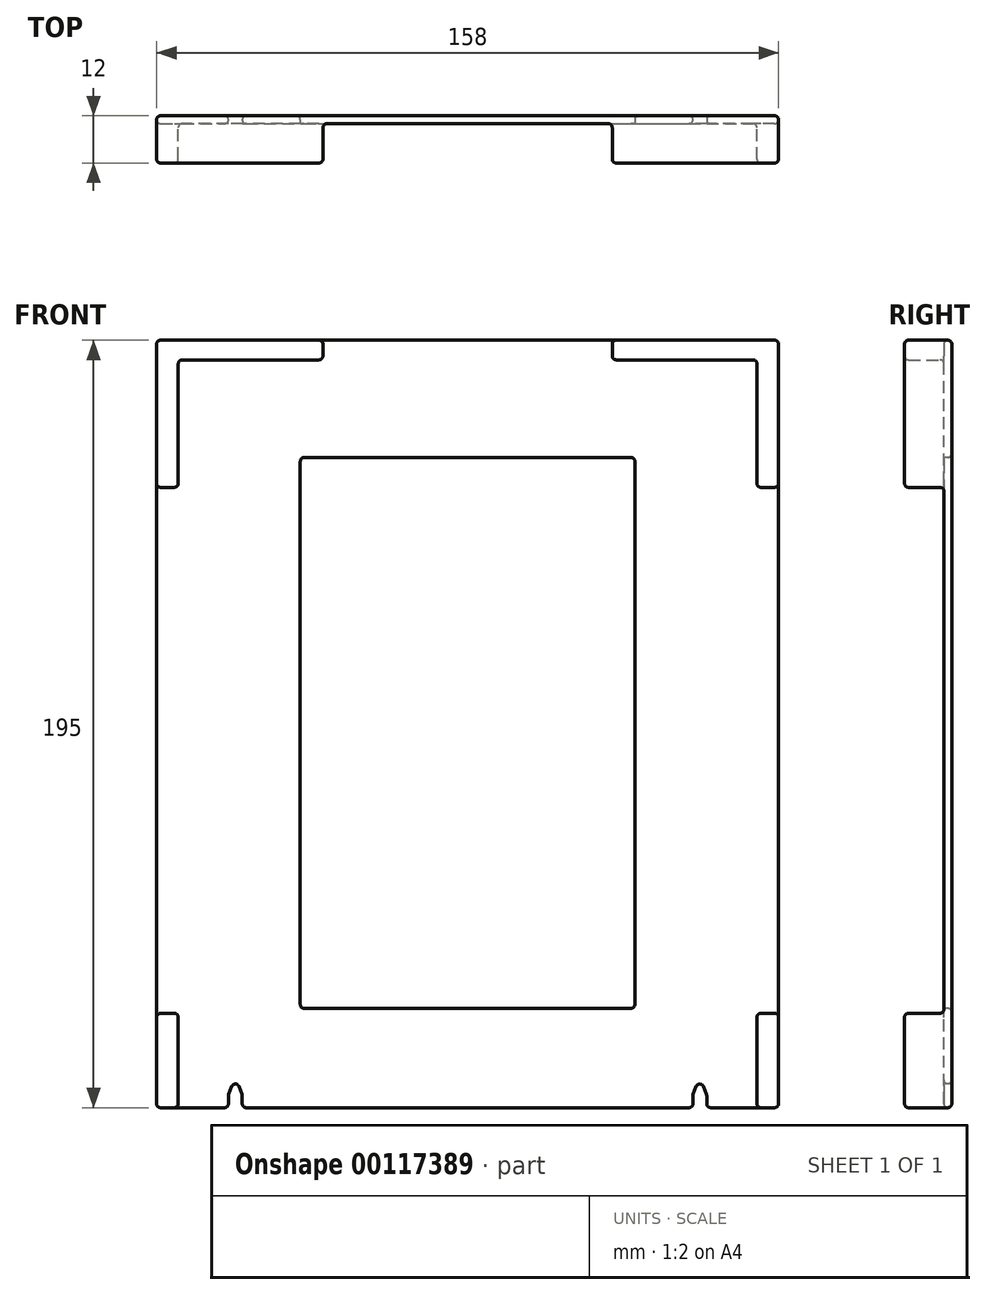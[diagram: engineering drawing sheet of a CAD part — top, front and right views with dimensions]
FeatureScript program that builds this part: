
annotation { "Feature Type Name" : "Feature", "Feature Type Description" : "" }
export const myFeature = defineFeature(function(context is Context, id is Id, definition is map)
    precondition{}
    {
        {
            var Q0;
            Q0=qCreatedBy(makeId("Front.planeOp"),FACE);
            var sketch = newSketch(context, id + "F0", { "sketchPlane" : qUnion([Q0])});
            skLineSegment(sketch, "E0.top", {"start": v(-73.5, 185) * mm, "end": v(-36.75, 185) * mm});
            skLineSegment(sketch, "E1.0", {"start": v(-79, 190) * mm, "end": v(0, 190) * mm});
            skLineSegment(sketch, "E1.1", {"start": v(-79, -5) * mm, "end": v(-79, 190) * mm});
            skLineSegment(sketch, "E1.2", {"start": v(-79, -5) * mm, "end": v(-60.75, -5) * mm});
            skLineSegment(sketch, "E2", {"start": v(-57.25, -1.81) * mm, "end": v(-57.25, -5) * mm});
            skLineSegment(sketch, "E3", {"start": v(-60.75, -1.81) * mm, "end": v(-60.75, -5) * mm});
            skLineSegment(sketch, "E4.trimOffspring", {"start": v(-57.25, -5) * mm, "end": v(0, -5) * mm});
            skArc(sketch, "E5", {"start": v(-58.06, 0.35) * mm, "mid": v(-59, 1) * mm, "end": v(-59.94, 0.35) * mm});
            skLineSegment(sketch, "E6", {"start": v(-58.06, 0.35) * mm, "end": v(-57.25, -1.81) * mm});
            skLineSegment(sketch, "E7", {"start": v(-59, 0) * mm, "end": v(-59, -2.66) * mm, "construction": true});
            skLineSegment(sketch, "E8.MirrorCS", {"start": v(-59.94, 0.35) * mm, "end": v(-60.75, -1.81) * mm});
            skLineSegment(sketch, "E9", {"start": v(0, -9.83) * mm, "end": v(0, 204.68) * mm, "construction": true});
            skPoint(sketch, "E9.startSnap0", {"position": v(0, -5) * mm});
            skLineSegment(sketch, "E10", {"start": v(-73.5, 185) * mm, "end": v(-73.5, 152.6) * mm});
            skLineSegment(sketch, "E11", {"start": v(-36.75, 185) * mm, "end": v(-36.75, 190) * mm});
            skLineSegment(sketch, "E12", {"start": v(-73.5, 152.6) * mm, "end": v(-79, 152.6) * mm});
            skLineSegment(sketch, "E13", {"start": v(-73.5, 18.97) * mm, "end": v(-79, 18.97) * mm});
            skPoint(sketch, "E14.orphan", {"position": v(0, 185) * mm});
            skLineSegment(sketch, "E15.trimOffspring", {"start": v(-73.5, 18.97) * mm, "end": v(-73.5, -5) * mm});
            skArc(sketch, "E16.MirrorCS", {"start": v(58.06, 0.35) * mm, "mid": v(59, 1) * mm, "end": v(59.94, 0.35) * mm});
            skLineSegment(sketch, "E17.MirrorCS", {"start": v(60.75, -1.81) * mm, "end": v(60.75, -5) * mm});
            skLineSegment(sketch, "E18.MirrorCS", {"start": v(57.25, -1.81) * mm, "end": v(57.25, -5) * mm});
            skLineSegment(sketch, "E19.MirrorCS", {"start": v(59.94, 0.35) * mm, "end": v(60.75, -1.81) * mm});
            skLineSegment(sketch, "E20.MirrorCS", {"start": v(59, 0) * mm, "end": v(59, -2.66) * mm, "construction": true});
            skLineSegment(sketch, "E21.MirrorCS", {"start": v(58.06, 0.35) * mm, "end": v(57.25, -1.81) * mm});
            skLineSegment(sketch, "E22.MirrorCS", {"start": v(73.5, 152.6) * mm, "end": v(79, 152.6) * mm});
            skLineSegment(sketch, "E23.MirrorCS", {"start": v(36.75, 185) * mm, "end": v(36.75, 190) * mm});
            skLineSegment(sketch, "E24.MirrorCS", {"start": v(73.5, 18.97) * mm, "end": v(79, 18.97) * mm});
            skLineSegment(sketch, "E25.MirrorCS", {"start": v(79, -5) * mm, "end": v(60.75, -5) * mm});
            skLineSegment(sketch, "E26.MirrorCS", {"start": v(73.5, 185) * mm, "end": v(73.5, 152.6) * mm});
            skLineSegment(sketch, "E27.MirrorCS", {"start": v(79, -5) * mm, "end": v(79, 190) * mm});
            skLineSegment(sketch, "E28.MirrorCS", {"start": v(79, 190) * mm, "end": v(0, 190) * mm});
            skLineSegment(sketch, "E29.MirrorCS", {"start": v(73.5, 185) * mm, "end": v(36.75, 185) * mm});
            skLineSegment(sketch, "E30.MirrorCS", {"start": v(57.25, -5) * mm, "end": v(0, -5) * mm});
            skLineSegment(sketch, "E31.MirrorCS", {"start": v(73.5, 18.97) * mm, "end": v(73.5, -5) * mm});
            skSolve(sketch);
        }
        {
            var Q0;
            Q0=makeQuery(id+"F0.imprint","IMPRINT",FACE,{"disambiguationData":[TD([[makeQuery(id+"F0.imprint","IMPRINT",EDGE,{"derivedFrom":sQuery(id+"F0.wireOp",EDGE,"E0.top")}),-1.0]])]});
            var Q1;
            Q1=makeQuery(id+"F0.imprint","IMPRINT",FACE,{"disambiguationData":[TD([[makeQuery(id+"F0.imprint","IMPRINT",EDGE,{"derivedFrom":sQuery(id+"F0.wireOp",EDGE,"E0.top")}),1.0]])]});
            var Q2;
            {var subQ1=sQuery(id+"F0.wireOp",EDGE,"E22.MirrorCS");Q2=makeQuery(id+"F0.imprint","IMPRINT",FACE,{"disambiguationData":[TD([[makeQuery(id+"F0.imprint","IMPRINT",EDGE,{"derivedFrom":subQ1}),1.0]])]});}
            var Q3;
            {var subQ0=sQuery(id+"F0.wireOp",EDGE,"E24.MirrorCS");Q3=makeQuery(id+"F0.imprint","IMPRINT",FACE,{"disambiguationData":[TD([[makeQuery(id+"F0.imprint","IMPRINT",EDGE,{"derivedFrom":subQ0}),-1.0]])]});}
            var Q4;
            {var subQ3=sQuery(id+"F0.wireOp",EDGE,"E13");Q4=makeQuery(id+"F0.imprint","IMPRINT",FACE,{"disambiguationData":[TD([[makeQuery(id+"F0.imprint","IMPRINT",EDGE,{"derivedFrom":subQ3}),1.0]])]});}
            extrude(context, id + "F1", {"entities" : qUnion([Q0, Q1, Q2, Q3, Q4]), "depth" : 2 * mm});
        }
        {
            var Q0;
            {var subQ1=sQuery(id+"F0.wireOp",EDGE,"E22.MirrorCS");Q0=makeQuery(id+"F0.imprint","IMPRINT",FACE,{"disambiguationData":[TD([[makeQuery(id+"F0.imprint","IMPRINT",EDGE,{"derivedFrom":subQ1}),1.0]])]});}
            var Q1;
            Q1=makeQuery(id+"F0.imprint","IMPRINT",FACE,{"disambiguationData":[TD([[makeQuery(id+"F0.imprint","IMPRINT",EDGE,{"derivedFrom":sQuery(id+"F0.wireOp",EDGE,"E0.top")}),1.0]])]});
            var Q2;
            {var subQ3=sQuery(id+"F0.wireOp",EDGE,"E13");Q2=makeQuery(id+"F0.imprint","IMPRINT",FACE,{"disambiguationData":[TD([[makeQuery(id+"F0.imprint","IMPRINT",EDGE,{"derivedFrom":subQ3}),1.0]])]});}
            var Q3;
            {var subQ0=sQuery(id+"F0.wireOp",EDGE,"E24.MirrorCS");Q3=makeQuery(id+"F0.imprint","IMPRINT",FACE,{"disambiguationData":[TD([[makeQuery(id+"F0.imprint","IMPRINT",EDGE,{"derivedFrom":subQ0}),-1.0]])]});}
            extrude(context, id + "F2", {"entities" : qUnion([Q0, Q1, Q2, Q3]), "operationType" : NewBodyOperationType.ADD, "depth" : 12 * mm});
        }
        {
            var Q0;
            Q0=makeQuery(id+"F1.opExtrude","CAP_FACE",FACE,{"disambiguationData":[OSD([sQuery(id+"F0.wireOp",EDGE,"E1.0"),sQuery(id+"F0.wireOp",EDGE,"E1.1"),sQuery(id+"F0.wireOp",EDGE,"E1.2"),sQuery(id+"F0.wireOp",EDGE,"E2"),sQuery(id+"F0.wireOp",EDGE,"E3"),sQuery(id+"F0.wireOp",EDGE,"E4.trimOffspring"),sQuery(id+"F0.wireOp",EDGE,"E5"),sQuery(id+"F0.wireOp",EDGE,"E6"),sQuery(id+"F0.wireOp",EDGE,"E8.MirrorCS"),sQuery(id+"F0.wireOp",EDGE,"E16.MirrorCS"),sQuery(id+"F0.wireOp",EDGE,"E17.MirrorCS"),sQuery(id+"F0.wireOp",EDGE,"E18.MirrorCS"),sQuery(id+"F0.wireOp",EDGE,"E19.MirrorCS"),sQuery(id+"F0.wireOp",EDGE,"E21.MirrorCS"),sQuery(id+"F0.wireOp",EDGE,"E25.MirrorCS"),sQuery(id+"F0.wireOp",EDGE,"E27.MirrorCS"),sQuery(id+"F0.wireOp",EDGE,"E28.MirrorCS"),sQuery(id+"F0.wireOp",EDGE,"E30.MirrorCS")])],"isStart":false});
            var sketch = newSketch(context, id + "F3", { "sketchPlane" : qUnion([Q0])});
            skLineSegment(sketch, "E32.bottom", {"start": v(-42.5, 160.22) * mm, "end": v(42.5, 160.22) * mm});
            skLineSegment(sketch, "E32.top", {"start": v(-42.5, 20.22) * mm, "end": v(42.5, 20.22) * mm});
            skLineSegment(sketch, "E32.left", {"start": v(-42.5, 160.22) * mm, "end": v(-42.5, 20.22) * mm});
            skLineSegment(sketch, "E32.right", {"start": v(42.5, 160.22) * mm, "end": v(42.5, 20.22) * mm});
            skSolve(sketch);
        }
        {
            var Q0;
            Q0 = qSketchRegion(id + "F3", true);
            extrude(context, id + "F4", {"entities" : qUnion([Q0]), "operationType" : NewBodyOperationType.REMOVE, "oppositeDirection" : true, "depth" : 25 * mm});
        }
        {
            var Q0;
            Q0=makeQuery(id+"F2.opExtrude","CAP_EDGE",EDGE,{"disambiguationData":[OSD([sQuery(id+"F0.wireOp",EDGE,"E29.MirrorCS")])],"isStart":false});
            var Q1;
            Q1=makeQuery(id+"F2.opExtrude","CAP_EDGE",EDGE,{"disambiguationData":[OSD([sQuery(id+"F0.wireOp",EDGE,"E10")])],"isStart":false});
            var Q2;
            Q2=makeQuery(id+"F4.boolean.opBoolean","COPY",EDGE,{"derivedFrom":makeQuery(id+"F4.opExtrude","CAP_EDGE",EDGE,{"disambiguationData":[OSD([sQuery(id+"F3.wireOp",EDGE,"E32.top")])],"isStart":true})});
            var Q3;
            Q3=makeQuery(id+"F2.opExtrude","CAP_EDGE",EDGE,{"disambiguationData":[OSD([sQuery(id+"F0.wireOp",EDGE,"E1.0")])],"isStart":false});
            var Q4;
            Q4=makeQuery(id+"F2.opExtrude","CAP_EDGE",EDGE,{"disambiguationData":[OSD([sQuery(id+"F0.wireOp",EDGE,"E28.MirrorCS")])],"isStart":false});
            var Q5;
            Q5=makeQuery(id+"F2.opExtrude","CAP_EDGE",EDGE,{"disambiguationData":[OSD([sQuery(id+"F0.wireOp",EDGE,"E31.MirrorCS")])],"isStart":false});
            var Q6;
            {var subQ0=sQuery(id+"F0.wireOp",EDGE,"E1.1");Q6=makeQuery(id+"F2.opExtrude","CAP_EDGE",EDGE,{"disambiguationData":[OSD([subQ0]),TDD([makeQuery(id+"F0.imprint","IMPRINT",EDGE,{"disambiguationData":[TD([[makeQuery(id+"F0.imprint","INTERSECT",VERTEX,{"derivedFrom":[sQuery(id+"F0.wireOp",EDGE,"E1.0"),subQ0]}),1.0]])],"derivedFrom":subQ0})])],"isStart":false});}
            var Q7;
            Q7=makeQuery(id+"F2.opExtrude","CAP_EDGE",EDGE,{"disambiguationData":[OSD([sQuery(id+"F0.wireOp",EDGE,"E23.MirrorCS")])],"isStart":false});
            var Q8;
            Q8=makeQuery(id+"F2.opExtrude","CAP_EDGE",EDGE,{"disambiguationData":[OSD([sQuery(id+"F0.wireOp",EDGE,"E15.trimOffspring")])],"isStart":false});
            var Q9;
            Q9=makeQuery(id+"F2.opExtrude","CAP_EDGE",EDGE,{"disambiguationData":[OSD([sQuery(id+"F0.wireOp",EDGE,"E24.MirrorCS")])],"isStart":false});
            var Q10;
            Q10=makeQuery(id+"F1.opExtrude","CAP_EDGE",EDGE,{"disambiguationData":[OSD([sQuery(id+"F0.wireOp",EDGE,"E17.MirrorCS")])],"isStart":false});
            var Q11;
            Q11=makeQuery(id+"F2.opExtrude","CAP_EDGE",EDGE,{"disambiguationData":[OSD([sQuery(id+"F0.wireOp",EDGE,"E1.2")])],"isStart":false});
            var Q12;
            Q12=makeQuery(id+"F1.opExtrude","SWEPT_EDGE",EDGE,{"disambiguationData":[OSD([sQuery(id+"F0.wireOp",EDGE,"E1.2"),sQuery(id+"F0.wireOp",EDGE,"E3")])]});
            var Q13;
            Q13=makeQuery(id+"F2.opExtrude","SWEPT_EDGE",EDGE,{"disambiguationData":[OSD([sQuery(id+"F0.wireOp",EDGE,"E26.MirrorCS"),sQuery(id+"F0.wireOp",EDGE,"E29.MirrorCS")])]});
            var Q14;
            Q14=makeQuery(id+"F1.opExtrude","CAP_EDGE",EDGE,{"disambiguationData":[OSD([sQuery(id+"F0.wireOp",EDGE,"E2")])],"isStart":false});
            var Q15;
            Q15=makeQuery(id+"F1.opExtrude","CAP_EDGE",EDGE,{"disambiguationData":[OSD([sQuery(id+"F0.wireOp",EDGE,"E4.trimOffspring"),sQuery(id+"F0.wireOp",EDGE,"E30.MirrorCS")])],"isStart":false});
            var Q16;
            Q16=makeQuery(id+"F2.opExtrude","CAP_EDGE",EDGE,{"disambiguationData":[OSD([sQuery(id+"F0.wireOp",EDGE,"E13")])],"isStart":false});
            var Q17;
            Q17=makeQuery(id+"F2.opExtrude","CAP_EDGE",EDGE,{"disambiguationData":[OSD([sQuery(id+"F0.wireOp",EDGE,"E0.top")])],"isStart":false});
            var Q18;
            {var subQ0=sQuery(id+"F0.wireOp",EDGE,"E27.MirrorCS");Q18=makeQuery(id+"F2.opExtrude","CAP_EDGE",EDGE,{"disambiguationData":[OSD([subQ0]),TDD([makeQuery(id+"F0.imprint","IMPRINT",EDGE,{"disambiguationData":[TD([[makeQuery(id+"F0.imprint","INTERSECT",VERTEX,{"derivedFrom":[sQuery(id+"F0.wireOp",EDGE,"E22.MirrorCS"),subQ0]}),-1.0]])],"derivedFrom":subQ0})])],"isStart":false});}
            var Q19;
            Q19=makeQuery(id+"F2.opExtrude","CAP_EDGE",EDGE,{"disambiguationData":[OSD([sQuery(id+"F0.wireOp",EDGE,"E26.MirrorCS")])],"isStart":false});
            var Q20;
            Q20=makeQuery(id+"F1.opExtrude","CAP_EDGE",EDGE,{"disambiguationData":[OSD([sQuery(id+"F0.wireOp",EDGE,"E27.MirrorCS")])],"isStart":false});
            var Q21;
            {var subQ0=sQuery(id+"F0.wireOp",EDGE,"E1.1");Q21=makeQuery(id+"F2.opExtrude","CAP_EDGE",EDGE,{"disambiguationData":[OSD([subQ0]),TDD([makeQuery(id+"F0.imprint","IMPRINT",EDGE,{"disambiguationData":[TD([[makeQuery(id+"F0.imprint","INTERSECT",VERTEX,{"derivedFrom":[subQ0,sQuery(id+"F0.wireOp",EDGE,"E1.2")]}),-1.0]])],"derivedFrom":subQ0})])],"isStart":false});}
            var Q22;
            Q22=makeQuery(id+"F1.opExtrude","CAP_EDGE",EDGE,{"disambiguationData":[OSD([sQuery(id+"F0.wireOp",EDGE,"E1.0"),sQuery(id+"F0.wireOp",EDGE,"E28.MirrorCS")])],"isStart":false});
            var Q23;
            Q23=makeQuery(id+"F1.opExtrude","CAP_EDGE",EDGE,{"disambiguationData":[OSD([sQuery(id+"F0.wireOp",EDGE,"E1.1")])],"isStart":false});
            var Q24;
            Q24=makeQuery(id+"F2.opExtrude","CAP_EDGE",EDGE,{"disambiguationData":[OSD([sQuery(id+"F0.wireOp",EDGE,"E25.MirrorCS")])],"isStart":false});
            var Q25;
            Q25=makeQuery(id+"F1.opExtrude","CAP_EDGE",EDGE,{"disambiguationData":[OSD([sQuery(id+"F0.wireOp",EDGE,"E1.2")])],"isStart":false});
            var Q26;
            Q26=makeQuery(id+"F1.opExtrude","CAP_EDGE",EDGE,{"disambiguationData":[OSD([sQuery(id+"F0.wireOp",EDGE,"E25.MirrorCS")])],"isStart":false});
            var Q27;
            Q27=makeQuery(id+"F2.opExtrude","CAP_EDGE",EDGE,{"disambiguationData":[OSD([sQuery(id+"F0.wireOp",EDGE,"E12")])],"isStart":false});
            var Q28;
            {var subQ0=sQuery(id+"F0.wireOp",EDGE,"E27.MirrorCS");Q28=makeQuery(id+"F2.opExtrude","CAP_EDGE",EDGE,{"disambiguationData":[OSD([subQ0]),TDD([makeQuery(id+"F0.imprint","IMPRINT",EDGE,{"disambiguationData":[TD([[makeQuery(id+"F0.imprint","INTERSECT",VERTEX,{"derivedFrom":[sQuery(id+"F0.wireOp",EDGE,"E24.MirrorCS"),subQ0]}),1.0]])],"derivedFrom":subQ0})])],"isStart":false});}
            var Q29;
            Q29=makeQuery(id+"F4.boolean.opBoolean","COPY",EDGE,{"derivedFrom":makeQuery(id+"F4.opExtrude","SWEPT_EDGE",EDGE,{"disambiguationData":[OSD([sQuery(id+"F3.wireOp",EDGE,"E32.top"),sQuery(id+"F3.wireOp",EDGE,"E32.left")])]})});
            var Q30;
            Q30=makeQuery(id+"F4.boolean.opBoolean","COPY",EDGE,{"derivedFrom":makeQuery(id+"F4.opExtrude","SWEPT_EDGE",EDGE,{"disambiguationData":[OSD([sQuery(id+"F3.wireOp",EDGE,"E32.top"),sQuery(id+"F3.wireOp",EDGE,"E32.right")])]})});
            var Q31;
            Q31=makeQuery(id+"F4.boolean.opBoolean","COPY",EDGE,{"derivedFrom":makeQuery(id+"F4.opExtrude","CAP_EDGE",EDGE,{"disambiguationData":[OSD([sQuery(id+"F3.wireOp",EDGE,"E32.bottom")])],"isStart":true})});
            var Q32;
            Q32=makeQuery(id+"F4.boolean.opBoolean","COPY",EDGE,{"derivedFrom":makeQuery(id+"F4.opExtrude","CAP_EDGE",EDGE,{"disambiguationData":[OSD([sQuery(id+"F3.wireOp",EDGE,"E32.left")])],"isStart":true})});
            var Q33;
            Q33=makeQuery(id+"F4.boolean.opBoolean","COPY",EDGE,{"derivedFrom":makeQuery(id+"F4.opExtrude","CAP_EDGE",EDGE,{"disambiguationData":[OSD([sQuery(id+"F3.wireOp",EDGE,"E32.right")])],"isStart":true})});
            var Q34;
            Q34=makeQuery(id+"F1.opExtrude","CAP_EDGE",EDGE,{"disambiguationData":[OSD([sQuery(id+"F0.wireOp",EDGE,"E6")])],"isStart":false});
            var Q35;
            Q35=makeQuery(id+"F1.opExtrude","SWEPT_EDGE",EDGE,{"disambiguationData":[OSD([sQuery(id+"F0.wireOp",EDGE,"E2"),sQuery(id+"F0.wireOp",EDGE,"E4.trimOffspring")])]});
            var Q36;
            Q36=makeQuery(id+"F1.opExtrude","CAP_EDGE",EDGE,{"disambiguationData":[OSD([sQuery(id+"F0.wireOp",EDGE,"E2")])],"isStart":true});
            var Q37;
            Q37=makeQuery(id+"F1.opExtrude","CAP_EDGE",EDGE,{"disambiguationData":[OSD([sQuery(id+"F0.wireOp",EDGE,"E4.trimOffspring"),sQuery(id+"F0.wireOp",EDGE,"E30.MirrorCS")])],"isStart":true});
            var Q38;
            Q38=makeQuery(id+"F1.opExtrude","CAP_EDGE",EDGE,{"disambiguationData":[OSD([sQuery(id+"F0.wireOp",EDGE,"E3")])],"isStart":false});
            var Q39;
            Q39=makeQuery(id+"F1.opExtrude","CAP_EDGE",EDGE,{"disambiguationData":[OSD([sQuery(id+"F0.wireOp",EDGE,"E16.MirrorCS")])],"isStart":false});
            var Q40;
            Q40=makeQuery(id+"F1.opExtrude","CAP_EDGE",EDGE,{"disambiguationData":[OSD([sQuery(id+"F0.wireOp",EDGE,"E8.MirrorCS")])],"isStart":false});
            var Q41;
            Q41=makeQuery(id+"F1.opExtrude","SWEPT_EDGE",EDGE,{"disambiguationData":[OSD([sQuery(id+"F0.wireOp",EDGE,"E17.MirrorCS"),sQuery(id+"F0.wireOp",EDGE,"E25.MirrorCS")])]});
            var Q42;
            Q42=makeQuery(id+"F1.opExtrude","SWEPT_EDGE",EDGE,{"disambiguationData":[OSD([sQuery(id+"F0.wireOp",EDGE,"E17.MirrorCS"),sQuery(id+"F0.wireOp",EDGE,"E19.MirrorCS")])]});
            var Q43;
            Q43=makeQuery(id+"F1.opExtrude","CAP_EDGE",EDGE,{"disambiguationData":[OSD([sQuery(id+"F0.wireOp",EDGE,"E19.MirrorCS")])],"isStart":false});
            var Q44;
            Q44=makeQuery(id+"F1.opExtrude","SWEPT_EDGE",EDGE,{"disambiguationData":[OSD([sQuery(id+"F0.wireOp",EDGE,"E2"),sQuery(id+"F0.wireOp",EDGE,"E6")])]});
            var Q45;
            Q45=makeQuery(id+"F2.boolean.opBoolean","INTERSECT",EDGE,{"derivedFrom":[makeQuery(id+"F1.opExtrude","CAP_FACE",FACE,{"disambiguationData":[OSD([sQuery(id+"F0.wireOp",EDGE,"E1.0"),sQuery(id+"F0.wireOp",EDGE,"E1.1"),sQuery(id+"F0.wireOp",EDGE,"E1.2"),sQuery(id+"F0.wireOp",EDGE,"E2"),sQuery(id+"F0.wireOp",EDGE,"E3"),sQuery(id+"F0.wireOp",EDGE,"E4.trimOffspring"),sQuery(id+"F0.wireOp",EDGE,"E5"),sQuery(id+"F0.wireOp",EDGE,"E6"),sQuery(id+"F0.wireOp",EDGE,"E8.MirrorCS"),sQuery(id+"F0.wireOp",EDGE,"E16.MirrorCS"),sQuery(id+"F0.wireOp",EDGE,"E17.MirrorCS"),sQuery(id+"F0.wireOp",EDGE,"E18.MirrorCS"),sQuery(id+"F0.wireOp",EDGE,"E19.MirrorCS"),sQuery(id+"F0.wireOp",EDGE,"E21.MirrorCS"),sQuery(id+"F0.wireOp",EDGE,"E25.MirrorCS"),sQuery(id+"F0.wireOp",EDGE,"E27.MirrorCS"),sQuery(id+"F0.wireOp",EDGE,"E28.MirrorCS"),sQuery(id+"F0.wireOp",EDGE,"E30.MirrorCS")])],"isStart":false}),makeQuery(id+"F2.opExtrude","SWEPT_FACE",FACE,{"disambiguationData":[OSD([sQuery(id+"F0.wireOp",EDGE,"E29.MirrorCS")])]})]});
            var Q46;
            Q46=makeQuery(id+"F2.opExtrude","SWEPT_EDGE",EDGE,{"disambiguationData":[OSD([sQuery(id+"F0.wireOp",EDGE,"E23.MirrorCS"),sQuery(id+"F0.wireOp",EDGE,"E29.MirrorCS")])]});
            var Q47;
            Q47=makeQuery(id+"F2.opExtrude","SWEPT_EDGE",EDGE,{"disambiguationData":[OSD([sQuery(id+"F0.wireOp",EDGE,"E1.2"),sQuery(id+"F0.wireOp",EDGE,"E15.trimOffspring")])]});
            var Q48;
            Q48=makeQuery(id+"F1.opExtrude","CAP_EDGE",EDGE,{"disambiguationData":[OSD([sQuery(id+"F0.wireOp",EDGE,"E5")])],"isStart":false});
            var Q49;
            Q49=makeQuery(id+"F2.boolean.opBoolean","INTERSECT",EDGE,{"derivedFrom":[makeQuery(id+"F1.opExtrude","CAP_FACE",FACE,{"disambiguationData":[OSD([sQuery(id+"F0.wireOp",EDGE,"E1.0"),sQuery(id+"F0.wireOp",EDGE,"E1.1"),sQuery(id+"F0.wireOp",EDGE,"E1.2"),sQuery(id+"F0.wireOp",EDGE,"E2"),sQuery(id+"F0.wireOp",EDGE,"E3"),sQuery(id+"F0.wireOp",EDGE,"E4.trimOffspring"),sQuery(id+"F0.wireOp",EDGE,"E5"),sQuery(id+"F0.wireOp",EDGE,"E6"),sQuery(id+"F0.wireOp",EDGE,"E8.MirrorCS"),sQuery(id+"F0.wireOp",EDGE,"E16.MirrorCS"),sQuery(id+"F0.wireOp",EDGE,"E17.MirrorCS"),sQuery(id+"F0.wireOp",EDGE,"E18.MirrorCS"),sQuery(id+"F0.wireOp",EDGE,"E19.MirrorCS"),sQuery(id+"F0.wireOp",EDGE,"E21.MirrorCS"),sQuery(id+"F0.wireOp",EDGE,"E25.MirrorCS"),sQuery(id+"F0.wireOp",EDGE,"E27.MirrorCS"),sQuery(id+"F0.wireOp",EDGE,"E28.MirrorCS"),sQuery(id+"F0.wireOp",EDGE,"E30.MirrorCS")])],"isStart":false}),makeQuery(id+"F2.opExtrude","SWEPT_FACE",FACE,{"disambiguationData":[OSD([sQuery(id+"F0.wireOp",EDGE,"E0.top")])]})]});
            var Q50;
            Q50=makeQuery(id+"F1.opExtrude","CAP_EDGE",EDGE,{"disambiguationData":[OSD([sQuery(id+"F0.wireOp",EDGE,"E18.MirrorCS")])],"isStart":false});
            var Q51;
            Q51=makeQuery(id+"F1.opExtrude","CAP_EDGE",EDGE,{"disambiguationData":[OSD([sQuery(id+"F0.wireOp",EDGE,"E21.MirrorCS")])],"isStart":false});
            var Q52;
            Q52=makeQuery(id+"F2.opExtrude","CAP_EDGE",EDGE,{"disambiguationData":[OSD([sQuery(id+"F0.wireOp",EDGE,"E11")])],"isStart":false});
            var Q53;
            Q53=makeQuery(id+"F2.boolean.opBoolean","INTERSECT",EDGE,{"derivedFrom":[makeQuery(id+"F1.opExtrude","CAP_FACE",FACE,{"disambiguationData":[OSD([sQuery(id+"F0.wireOp",EDGE,"E1.0"),sQuery(id+"F0.wireOp",EDGE,"E1.1"),sQuery(id+"F0.wireOp",EDGE,"E1.2"),sQuery(id+"F0.wireOp",EDGE,"E2"),sQuery(id+"F0.wireOp",EDGE,"E3"),sQuery(id+"F0.wireOp",EDGE,"E4.trimOffspring"),sQuery(id+"F0.wireOp",EDGE,"E5"),sQuery(id+"F0.wireOp",EDGE,"E6"),sQuery(id+"F0.wireOp",EDGE,"E8.MirrorCS"),sQuery(id+"F0.wireOp",EDGE,"E16.MirrorCS"),sQuery(id+"F0.wireOp",EDGE,"E17.MirrorCS"),sQuery(id+"F0.wireOp",EDGE,"E18.MirrorCS"),sQuery(id+"F0.wireOp",EDGE,"E19.MirrorCS"),sQuery(id+"F0.wireOp",EDGE,"E21.MirrorCS"),sQuery(id+"F0.wireOp",EDGE,"E25.MirrorCS"),sQuery(id+"F0.wireOp",EDGE,"E27.MirrorCS"),sQuery(id+"F0.wireOp",EDGE,"E28.MirrorCS"),sQuery(id+"F0.wireOp",EDGE,"E30.MirrorCS")])],"isStart":false}),makeQuery(id+"F2.opExtrude","SWEPT_FACE",FACE,{"disambiguationData":[OSD([sQuery(id+"F0.wireOp",EDGE,"E31.MirrorCS")])]})]});
            var Q54;
            Q54=makeQuery(id+"F2.opExtrude","SWEPT_EDGE",EDGE,{"disambiguationData":[OSD([sQuery(id+"F0.wireOp",EDGE,"E23.MirrorCS"),sQuery(id+"F0.wireOp",EDGE,"E28.MirrorCS")])]});
            var Q55;
            Q55=makeQuery(id+"F2.boolean.opBoolean","INTERSECT",EDGE,{"derivedFrom":[makeQuery(id+"F1.opExtrude","CAP_FACE",FACE,{"disambiguationData":[OSD([sQuery(id+"F0.wireOp",EDGE,"E1.0"),sQuery(id+"F0.wireOp",EDGE,"E1.1"),sQuery(id+"F0.wireOp",EDGE,"E1.2"),sQuery(id+"F0.wireOp",EDGE,"E2"),sQuery(id+"F0.wireOp",EDGE,"E3"),sQuery(id+"F0.wireOp",EDGE,"E4.trimOffspring"),sQuery(id+"F0.wireOp",EDGE,"E5"),sQuery(id+"F0.wireOp",EDGE,"E6"),sQuery(id+"F0.wireOp",EDGE,"E8.MirrorCS"),sQuery(id+"F0.wireOp",EDGE,"E16.MirrorCS"),sQuery(id+"F0.wireOp",EDGE,"E17.MirrorCS"),sQuery(id+"F0.wireOp",EDGE,"E18.MirrorCS"),sQuery(id+"F0.wireOp",EDGE,"E19.MirrorCS"),sQuery(id+"F0.wireOp",EDGE,"E21.MirrorCS"),sQuery(id+"F0.wireOp",EDGE,"E25.MirrorCS"),sQuery(id+"F0.wireOp",EDGE,"E27.MirrorCS"),sQuery(id+"F0.wireOp",EDGE,"E28.MirrorCS"),sQuery(id+"F0.wireOp",EDGE,"E30.MirrorCS")])],"isStart":false}),makeQuery(id+"F2.opExtrude","SWEPT_FACE",FACE,{"disambiguationData":[OSD([sQuery(id+"F0.wireOp",EDGE,"E10")])]})]});
            var Q56;
            Q56=makeQuery(id+"F2.opExtrude","SWEPT_EDGE",EDGE,{"disambiguationData":[OSD([sQuery(id+"F0.wireOp",EDGE,"E1.1"),sQuery(id+"F0.wireOp",EDGE,"E12")])]});
            var Q57;
            Q57=makeQuery(id+"F2.opExtrude","SWEPT_EDGE",EDGE,{"disambiguationData":[OSD([sQuery(id+"F0.wireOp",EDGE,"E0.top"),sQuery(id+"F0.wireOp",EDGE,"E10")])]});
            var Q58;
            Q58=makeQuery(id+"F2.boolean.opBoolean","INTERSECT",EDGE,{"derivedFrom":[makeQuery(id+"F1.opExtrude","CAP_FACE",FACE,{"disambiguationData":[OSD([sQuery(id+"F0.wireOp",EDGE,"E1.0"),sQuery(id+"F0.wireOp",EDGE,"E1.1"),sQuery(id+"F0.wireOp",EDGE,"E1.2"),sQuery(id+"F0.wireOp",EDGE,"E2"),sQuery(id+"F0.wireOp",EDGE,"E3"),sQuery(id+"F0.wireOp",EDGE,"E4.trimOffspring"),sQuery(id+"F0.wireOp",EDGE,"E5"),sQuery(id+"F0.wireOp",EDGE,"E6"),sQuery(id+"F0.wireOp",EDGE,"E8.MirrorCS"),sQuery(id+"F0.wireOp",EDGE,"E16.MirrorCS"),sQuery(id+"F0.wireOp",EDGE,"E17.MirrorCS"),sQuery(id+"F0.wireOp",EDGE,"E18.MirrorCS"),sQuery(id+"F0.wireOp",EDGE,"E19.MirrorCS"),sQuery(id+"F0.wireOp",EDGE,"E21.MirrorCS"),sQuery(id+"F0.wireOp",EDGE,"E25.MirrorCS"),sQuery(id+"F0.wireOp",EDGE,"E27.MirrorCS"),sQuery(id+"F0.wireOp",EDGE,"E28.MirrorCS"),sQuery(id+"F0.wireOp",EDGE,"E30.MirrorCS")])],"isStart":false}),makeQuery(id+"F2.opExtrude","SWEPT_FACE",FACE,{"disambiguationData":[OSD([sQuery(id+"F0.wireOp",EDGE,"E13")])]})]});
            var Q59;
            {var subQ0=sQuery(id+"F0.wireOp",EDGE,"E1.1");var subQ1=sQuery(id+"F0.wireOp",EDGE,"E1.0");Q59=makeQuery(id+"F2.boolean.opBoolean","MERGE",EDGE,{"derivedFrom":[makeQuery(id+"F1.opExtrude","SWEPT_EDGE",EDGE,{"disambiguationData":[OSD([subQ1,subQ0])]}),makeQuery(id+"F2.opExtrude","SWEPT_EDGE",EDGE,{"disambiguationData":[OSD([subQ1,subQ0])]})]});}
            var Q60;
            {var subQ0=sQuery(id+"F0.wireOp",EDGE,"E1.2");var subQ1=sQuery(id+"F0.wireOp",EDGE,"E1.1");Q60=makeQuery(id+"F2.boolean.opBoolean","MERGE",EDGE,{"derivedFrom":[makeQuery(id+"F1.opExtrude","SWEPT_EDGE",EDGE,{"disambiguationData":[OSD([subQ1,subQ0])]}),makeQuery(id+"F2.opExtrude","SWEPT_EDGE",EDGE,{"disambiguationData":[OSD([subQ1,subQ0])]})]});}
            var Q61;
            {var subQ0=sQuery(id+"F0.wireOp",EDGE,"E27.MirrorCS");var subQ1=sQuery(id+"F0.wireOp",EDGE,"E25.MirrorCS");Q61=makeQuery(id+"F2.boolean.opBoolean","MERGE",EDGE,{"derivedFrom":[makeQuery(id+"F1.opExtrude","SWEPT_EDGE",EDGE,{"disambiguationData":[OSD([subQ1,subQ0])]}),makeQuery(id+"F2.opExtrude","SWEPT_EDGE",EDGE,{"disambiguationData":[OSD([subQ1,subQ0])]})]});}
            var Q62;
            {var subQ0=sQuery(id+"F0.wireOp",EDGE,"E28.MirrorCS");var subQ1=sQuery(id+"F0.wireOp",EDGE,"E27.MirrorCS");Q62=makeQuery(id+"F2.boolean.opBoolean","MERGE",EDGE,{"derivedFrom":[makeQuery(id+"F1.opExtrude","SWEPT_EDGE",EDGE,{"disambiguationData":[OSD([subQ1,subQ0])]}),makeQuery(id+"F2.opExtrude","SWEPT_EDGE",EDGE,{"disambiguationData":[OSD([subQ1,subQ0])]})]});}
            var Q63;
            Q63=makeQuery(id+"F1.opExtrude","CAP_EDGE",EDGE,{"disambiguationData":[OSD([sQuery(id+"F0.wireOp",EDGE,"E1.0"),sQuery(id+"F0.wireOp",EDGE,"E28.MirrorCS")])],"isStart":true});
            var Q64;
            Q64=makeQuery(id+"F2.opExtrude","CAP_EDGE",EDGE,{"disambiguationData":[OSD([sQuery(id+"F0.wireOp",EDGE,"E22.MirrorCS")])],"isStart":false});
            var Q65;
            Q65=makeQuery(id+"F1.opExtrude","CAP_EDGE",EDGE,{"disambiguationData":[OSD([sQuery(id+"F0.wireOp",EDGE,"E1.1")])],"isStart":true});
            var Q66;
            Q66=makeQuery(id+"F1.opExtrude","CAP_EDGE",EDGE,{"disambiguationData":[OSD([sQuery(id+"F0.wireOp",EDGE,"E1.2")])],"isStart":true});
            var Q67;
            Q67=makeQuery(id+"F1.opExtrude","CAP_EDGE",EDGE,{"disambiguationData":[OSD([sQuery(id+"F0.wireOp",EDGE,"E25.MirrorCS")])],"isStart":true});
            var Q68;
            Q68=makeQuery(id+"F1.opExtrude","CAP_EDGE",EDGE,{"disambiguationData":[OSD([sQuery(id+"F0.wireOp",EDGE,"E27.MirrorCS")])],"isStart":true});
            var Q69;
            Q69=makeQuery(id+"F2.opExtrude","SWEPT_EDGE",EDGE,{"disambiguationData":[OSD([sQuery(id+"F0.wireOp",EDGE,"E24.MirrorCS"),sQuery(id+"F0.wireOp",EDGE,"E31.MirrorCS")])]});
            var Q70;
            Q70=makeQuery(id+"F2.opExtrude","SWEPT_EDGE",EDGE,{"disambiguationData":[OSD([sQuery(id+"F0.wireOp",EDGE,"E13"),sQuery(id+"F0.wireOp",EDGE,"E15.trimOffspring")])]});
            var Q71;
            Q71=makeQuery(id+"F2.opExtrude","SWEPT_EDGE",EDGE,{"disambiguationData":[OSD([sQuery(id+"F0.wireOp",EDGE,"E24.MirrorCS"),sQuery(id+"F0.wireOp",EDGE,"E27.MirrorCS")])]});
            var Q72;
            Q72=makeQuery(id+"F2.boolean.opBoolean","INTERSECT",EDGE,{"derivedFrom":[makeQuery(id+"F1.opExtrude","CAP_FACE",FACE,{"disambiguationData":[OSD([sQuery(id+"F0.wireOp",EDGE,"E1.0"),sQuery(id+"F0.wireOp",EDGE,"E1.1"),sQuery(id+"F0.wireOp",EDGE,"E1.2"),sQuery(id+"F0.wireOp",EDGE,"E2"),sQuery(id+"F0.wireOp",EDGE,"E3"),sQuery(id+"F0.wireOp",EDGE,"E4.trimOffspring"),sQuery(id+"F0.wireOp",EDGE,"E5"),sQuery(id+"F0.wireOp",EDGE,"E6"),sQuery(id+"F0.wireOp",EDGE,"E8.MirrorCS"),sQuery(id+"F0.wireOp",EDGE,"E16.MirrorCS"),sQuery(id+"F0.wireOp",EDGE,"E17.MirrorCS"),sQuery(id+"F0.wireOp",EDGE,"E18.MirrorCS"),sQuery(id+"F0.wireOp",EDGE,"E19.MirrorCS"),sQuery(id+"F0.wireOp",EDGE,"E21.MirrorCS"),sQuery(id+"F0.wireOp",EDGE,"E25.MirrorCS"),sQuery(id+"F0.wireOp",EDGE,"E27.MirrorCS"),sQuery(id+"F0.wireOp",EDGE,"E28.MirrorCS"),sQuery(id+"F0.wireOp",EDGE,"E30.MirrorCS")])],"isStart":false}),makeQuery(id+"F2.opExtrude","SWEPT_FACE",FACE,{"disambiguationData":[OSD([sQuery(id+"F0.wireOp",EDGE,"E26.MirrorCS")])]})]});
            var Q73;
            Q73=makeQuery(id+"F2.opExtrude","SWEPT_EDGE",EDGE,{"disambiguationData":[OSD([sQuery(id+"F0.wireOp",EDGE,"E1.1"),sQuery(id+"F0.wireOp",EDGE,"E13")])]});
            var Q74;
            Q74=makeQuery(id+"F2.opExtrude","SWEPT_EDGE",EDGE,{"disambiguationData":[OSD([sQuery(id+"F0.wireOp",EDGE,"E25.MirrorCS"),sQuery(id+"F0.wireOp",EDGE,"E31.MirrorCS")])]});
            var Q75;
            Q75=makeQuery(id+"F2.opExtrude","SWEPT_EDGE",EDGE,{"disambiguationData":[OSD([sQuery(id+"F0.wireOp",EDGE,"E10"),sQuery(id+"F0.wireOp",EDGE,"E12")])]});
            var Q76;
            Q76=makeQuery(id+"F4.boolean.opBoolean","COPY",EDGE,{"derivedFrom":makeQuery(id+"F4.opExtrude","SWEPT_EDGE",EDGE,{"disambiguationData":[OSD([sQuery(id+"F3.wireOp",EDGE,"E32.bottom"),sQuery(id+"F3.wireOp",EDGE,"E32.right")])]})});
            var Q77;
            Q77=makeQuery(id+"F4.boolean.opBoolean","INTERSECT",EDGE,{"derivedFrom":[makeQuery(id+"F1.opExtrude","CAP_FACE",FACE,{"disambiguationData":[OSD([sQuery(id+"F0.wireOp",EDGE,"E1.0"),sQuery(id+"F0.wireOp",EDGE,"E1.1"),sQuery(id+"F0.wireOp",EDGE,"E1.2"),sQuery(id+"F0.wireOp",EDGE,"E2"),sQuery(id+"F0.wireOp",EDGE,"E3"),sQuery(id+"F0.wireOp",EDGE,"E4.trimOffspring"),sQuery(id+"F0.wireOp",EDGE,"E5"),sQuery(id+"F0.wireOp",EDGE,"E6"),sQuery(id+"F0.wireOp",EDGE,"E8.MirrorCS"),sQuery(id+"F0.wireOp",EDGE,"E16.MirrorCS"),sQuery(id+"F0.wireOp",EDGE,"E17.MirrorCS"),sQuery(id+"F0.wireOp",EDGE,"E18.MirrorCS"),sQuery(id+"F0.wireOp",EDGE,"E19.MirrorCS"),sQuery(id+"F0.wireOp",EDGE,"E21.MirrorCS"),sQuery(id+"F0.wireOp",EDGE,"E25.MirrorCS"),sQuery(id+"F0.wireOp",EDGE,"E27.MirrorCS"),sQuery(id+"F0.wireOp",EDGE,"E28.MirrorCS"),sQuery(id+"F0.wireOp",EDGE,"E30.MirrorCS")])],"isStart":true}),makeQuery(id+"F4.opExtrude","SWEPT_FACE",FACE,{"disambiguationData":[OSD([sQuery(id+"F3.wireOp",EDGE,"E32.bottom")])]})]});
            var Q78;
            Q78=makeQuery(id+"F4.boolean.opBoolean","INTERSECT",EDGE,{"derivedFrom":[makeQuery(id+"F1.opExtrude","CAP_FACE",FACE,{"disambiguationData":[OSD([sQuery(id+"F0.wireOp",EDGE,"E1.0"),sQuery(id+"F0.wireOp",EDGE,"E1.1"),sQuery(id+"F0.wireOp",EDGE,"E1.2"),sQuery(id+"F0.wireOp",EDGE,"E2"),sQuery(id+"F0.wireOp",EDGE,"E3"),sQuery(id+"F0.wireOp",EDGE,"E4.trimOffspring"),sQuery(id+"F0.wireOp",EDGE,"E5"),sQuery(id+"F0.wireOp",EDGE,"E6"),sQuery(id+"F0.wireOp",EDGE,"E8.MirrorCS"),sQuery(id+"F0.wireOp",EDGE,"E16.MirrorCS"),sQuery(id+"F0.wireOp",EDGE,"E17.MirrorCS"),sQuery(id+"F0.wireOp",EDGE,"E18.MirrorCS"),sQuery(id+"F0.wireOp",EDGE,"E19.MirrorCS"),sQuery(id+"F0.wireOp",EDGE,"E21.MirrorCS"),sQuery(id+"F0.wireOp",EDGE,"E25.MirrorCS"),sQuery(id+"F0.wireOp",EDGE,"E27.MirrorCS"),sQuery(id+"F0.wireOp",EDGE,"E28.MirrorCS"),sQuery(id+"F0.wireOp",EDGE,"E30.MirrorCS")])],"isStart":true}),makeQuery(id+"F4.opExtrude","SWEPT_FACE",FACE,{"disambiguationData":[OSD([sQuery(id+"F3.wireOp",EDGE,"E32.top")])]})]});
            var Q79;
            Q79=makeQuery(id+"F4.boolean.opBoolean","INTERSECT",EDGE,{"derivedFrom":[makeQuery(id+"F1.opExtrude","CAP_FACE",FACE,{"disambiguationData":[OSD([sQuery(id+"F0.wireOp",EDGE,"E1.0"),sQuery(id+"F0.wireOp",EDGE,"E1.1"),sQuery(id+"F0.wireOp",EDGE,"E1.2"),sQuery(id+"F0.wireOp",EDGE,"E2"),sQuery(id+"F0.wireOp",EDGE,"E3"),sQuery(id+"F0.wireOp",EDGE,"E4.trimOffspring"),sQuery(id+"F0.wireOp",EDGE,"E5"),sQuery(id+"F0.wireOp",EDGE,"E6"),sQuery(id+"F0.wireOp",EDGE,"E8.MirrorCS"),sQuery(id+"F0.wireOp",EDGE,"E16.MirrorCS"),sQuery(id+"F0.wireOp",EDGE,"E17.MirrorCS"),sQuery(id+"F0.wireOp",EDGE,"E18.MirrorCS"),sQuery(id+"F0.wireOp",EDGE,"E19.MirrorCS"),sQuery(id+"F0.wireOp",EDGE,"E21.MirrorCS"),sQuery(id+"F0.wireOp",EDGE,"E25.MirrorCS"),sQuery(id+"F0.wireOp",EDGE,"E27.MirrorCS"),sQuery(id+"F0.wireOp",EDGE,"E28.MirrorCS"),sQuery(id+"F0.wireOp",EDGE,"E30.MirrorCS")])],"isStart":true}),makeQuery(id+"F4.opExtrude","SWEPT_FACE",FACE,{"disambiguationData":[OSD([sQuery(id+"F3.wireOp",EDGE,"E32.right")])]})]});
            var Q80;
            Q80=makeQuery(id+"F4.boolean.opBoolean","COPY",EDGE,{"derivedFrom":makeQuery(id+"F4.opExtrude","SWEPT_EDGE",EDGE,{"disambiguationData":[OSD([sQuery(id+"F3.wireOp",EDGE,"E32.bottom"),sQuery(id+"F3.wireOp",EDGE,"E32.left")])]})});
            var Q81;
            Q81=makeQuery(id+"F1.opExtrude","SWEPT_EDGE",EDGE,{"disambiguationData":[OSD([sQuery(id+"F0.wireOp",EDGE,"E16.MirrorCS"),sQuery(id+"F0.wireOp",EDGE,"E21.MirrorCS")])]});
            var Q82;
            Q82=makeQuery(id+"F1.opExtrude","CAP_EDGE",EDGE,{"disambiguationData":[OSD([sQuery(id+"F0.wireOp",EDGE,"E18.MirrorCS")])],"isStart":true});
            var Q83;
            Q83=makeQuery(id+"F1.opExtrude","SWEPT_EDGE",EDGE,{"disambiguationData":[OSD([sQuery(id+"F0.wireOp",EDGE,"E3"),sQuery(id+"F0.wireOp",EDGE,"E8.MirrorCS")])]});
            var Q84;
            Q84=makeQuery(id+"F1.opExtrude","SWEPT_EDGE",EDGE,{"disambiguationData":[OSD([sQuery(id+"F0.wireOp",EDGE,"E18.MirrorCS"),sQuery(id+"F0.wireOp",EDGE,"E21.MirrorCS")])]});
            var Q85;
            Q85=makeQuery(id+"F1.opExtrude","CAP_EDGE",EDGE,{"disambiguationData":[OSD([sQuery(id+"F0.wireOp",EDGE,"E19.MirrorCS")])],"isStart":true});
            var Q86;
            Q86=makeQuery(id+"F1.opExtrude","SWEPT_EDGE",EDGE,{"disambiguationData":[OSD([sQuery(id+"F0.wireOp",EDGE,"E16.MirrorCS"),sQuery(id+"F0.wireOp",EDGE,"E19.MirrorCS")])]});
            var Q87;
            Q87=makeQuery(id+"F1.opExtrude","CAP_EDGE",EDGE,{"disambiguationData":[OSD([sQuery(id+"F0.wireOp",EDGE,"E3")])],"isStart":true});
            var Q88;
            Q88=makeQuery(id+"F1.opExtrude","SWEPT_EDGE",EDGE,{"disambiguationData":[OSD([sQuery(id+"F0.wireOp",EDGE,"E5"),sQuery(id+"F0.wireOp",EDGE,"E6")])]});
            var Q89;
            Q89=makeQuery(id+"F1.opExtrude","SWEPT_EDGE",EDGE,{"disambiguationData":[OSD([sQuery(id+"F0.wireOp",EDGE,"E5"),sQuery(id+"F0.wireOp",EDGE,"E8.MirrorCS")])]});
            var Q90;
            Q90=makeQuery(id+"F1.opExtrude","CAP_EDGE",EDGE,{"disambiguationData":[OSD([sQuery(id+"F0.wireOp",EDGE,"E21.MirrorCS")])],"isStart":true});
            var Q91;
            Q91=makeQuery(id+"F1.opExtrude","CAP_EDGE",EDGE,{"disambiguationData":[OSD([sQuery(id+"F0.wireOp",EDGE,"E6")])],"isStart":true});
            var Q92;
            Q92=makeQuery(id+"F1.opExtrude","SWEPT_EDGE",EDGE,{"disambiguationData":[OSD([sQuery(id+"F0.wireOp",EDGE,"E18.MirrorCS"),sQuery(id+"F0.wireOp",EDGE,"E30.MirrorCS")])]});
            var Q93;
            Q93=makeQuery(id+"F1.opExtrude","CAP_EDGE",EDGE,{"disambiguationData":[OSD([sQuery(id+"F0.wireOp",EDGE,"E8.MirrorCS")])],"isStart":true});
            var Q94;
            Q94=makeQuery(id+"F1.opExtrude","CAP_EDGE",EDGE,{"disambiguationData":[OSD([sQuery(id+"F0.wireOp",EDGE,"E17.MirrorCS")])],"isStart":true});
            var Q95;
            Q95=makeQuery(id+"F2.boolean.opBoolean","INTERSECT",EDGE,{"derivedFrom":[makeQuery(id+"F1.opExtrude","CAP_FACE",FACE,{"disambiguationData":[OSD([sQuery(id+"F0.wireOp",EDGE,"E1.0"),sQuery(id+"F0.wireOp",EDGE,"E1.1"),sQuery(id+"F0.wireOp",EDGE,"E1.2"),sQuery(id+"F0.wireOp",EDGE,"E2"),sQuery(id+"F0.wireOp",EDGE,"E3"),sQuery(id+"F0.wireOp",EDGE,"E4.trimOffspring"),sQuery(id+"F0.wireOp",EDGE,"E5"),sQuery(id+"F0.wireOp",EDGE,"E6"),sQuery(id+"F0.wireOp",EDGE,"E8.MirrorCS"),sQuery(id+"F0.wireOp",EDGE,"E16.MirrorCS"),sQuery(id+"F0.wireOp",EDGE,"E17.MirrorCS"),sQuery(id+"F0.wireOp",EDGE,"E18.MirrorCS"),sQuery(id+"F0.wireOp",EDGE,"E19.MirrorCS"),sQuery(id+"F0.wireOp",EDGE,"E21.MirrorCS"),sQuery(id+"F0.wireOp",EDGE,"E25.MirrorCS"),sQuery(id+"F0.wireOp",EDGE,"E27.MirrorCS"),sQuery(id+"F0.wireOp",EDGE,"E28.MirrorCS"),sQuery(id+"F0.wireOp",EDGE,"E30.MirrorCS")])],"isStart":false}),makeQuery(id+"F2.opExtrude","SWEPT_FACE",FACE,{"disambiguationData":[OSD([sQuery(id+"F0.wireOp",EDGE,"E23.MirrorCS")])]})]});
            var Q96;
            Q96=makeQuery(id+"F2.opExtrude","SWEPT_EDGE",EDGE,{"disambiguationData":[OSD([sQuery(id+"F0.wireOp",EDGE,"E1.0"),sQuery(id+"F0.wireOp",EDGE,"E11")])]});
            var Q97;
            Q97=makeQuery(id+"F2.boolean.opBoolean","INTERSECT",EDGE,{"derivedFrom":[makeQuery(id+"F1.opExtrude","CAP_FACE",FACE,{"disambiguationData":[OSD([sQuery(id+"F0.wireOp",EDGE,"E1.0"),sQuery(id+"F0.wireOp",EDGE,"E1.1"),sQuery(id+"F0.wireOp",EDGE,"E1.2"),sQuery(id+"F0.wireOp",EDGE,"E2"),sQuery(id+"F0.wireOp",EDGE,"E3"),sQuery(id+"F0.wireOp",EDGE,"E4.trimOffspring"),sQuery(id+"F0.wireOp",EDGE,"E5"),sQuery(id+"F0.wireOp",EDGE,"E6"),sQuery(id+"F0.wireOp",EDGE,"E8.MirrorCS"),sQuery(id+"F0.wireOp",EDGE,"E16.MirrorCS"),sQuery(id+"F0.wireOp",EDGE,"E17.MirrorCS"),sQuery(id+"F0.wireOp",EDGE,"E18.MirrorCS"),sQuery(id+"F0.wireOp",EDGE,"E19.MirrorCS"),sQuery(id+"F0.wireOp",EDGE,"E21.MirrorCS"),sQuery(id+"F0.wireOp",EDGE,"E25.MirrorCS"),sQuery(id+"F0.wireOp",EDGE,"E27.MirrorCS"),sQuery(id+"F0.wireOp",EDGE,"E28.MirrorCS"),sQuery(id+"F0.wireOp",EDGE,"E30.MirrorCS")])],"isStart":false}),makeQuery(id+"F2.opExtrude","SWEPT_FACE",FACE,{"disambiguationData":[OSD([sQuery(id+"F0.wireOp",EDGE,"E12")])]})]});
            var Q98;
            Q98=makeQuery(id+"F2.opExtrude","SWEPT_EDGE",EDGE,{"disambiguationData":[OSD([sQuery(id+"F0.wireOp",EDGE,"E22.MirrorCS"),sQuery(id+"F0.wireOp",EDGE,"E26.MirrorCS")])]});
            var Q99;
            Q99=makeQuery(id+"F2.boolean.opBoolean","INTERSECT",EDGE,{"derivedFrom":[makeQuery(id+"F1.opExtrude","CAP_FACE",FACE,{"disambiguationData":[OSD([sQuery(id+"F0.wireOp",EDGE,"E1.0"),sQuery(id+"F0.wireOp",EDGE,"E1.1"),sQuery(id+"F0.wireOp",EDGE,"E1.2"),sQuery(id+"F0.wireOp",EDGE,"E2"),sQuery(id+"F0.wireOp",EDGE,"E3"),sQuery(id+"F0.wireOp",EDGE,"E4.trimOffspring"),sQuery(id+"F0.wireOp",EDGE,"E5"),sQuery(id+"F0.wireOp",EDGE,"E6"),sQuery(id+"F0.wireOp",EDGE,"E8.MirrorCS"),sQuery(id+"F0.wireOp",EDGE,"E16.MirrorCS"),sQuery(id+"F0.wireOp",EDGE,"E17.MirrorCS"),sQuery(id+"F0.wireOp",EDGE,"E18.MirrorCS"),sQuery(id+"F0.wireOp",EDGE,"E19.MirrorCS"),sQuery(id+"F0.wireOp",EDGE,"E21.MirrorCS"),sQuery(id+"F0.wireOp",EDGE,"E25.MirrorCS"),sQuery(id+"F0.wireOp",EDGE,"E27.MirrorCS"),sQuery(id+"F0.wireOp",EDGE,"E28.MirrorCS"),sQuery(id+"F0.wireOp",EDGE,"E30.MirrorCS")])],"isStart":false}),makeQuery(id+"F2.opExtrude","SWEPT_FACE",FACE,{"disambiguationData":[OSD([sQuery(id+"F0.wireOp",EDGE,"E24.MirrorCS")])]})]});
            var Q100;
            Q100=makeQuery(id+"F2.opExtrude","SWEPT_EDGE",EDGE,{"disambiguationData":[OSD([sQuery(id+"F0.wireOp",EDGE,"E0.top"),sQuery(id+"F0.wireOp",EDGE,"E11")])]});
            var Q101;
            Q101=makeQuery(id+"F2.boolean.opBoolean","INTERSECT",EDGE,{"derivedFrom":[makeQuery(id+"F1.opExtrude","CAP_FACE",FACE,{"disambiguationData":[OSD([sQuery(id+"F0.wireOp",EDGE,"E1.0"),sQuery(id+"F0.wireOp",EDGE,"E1.1"),sQuery(id+"F0.wireOp",EDGE,"E1.2"),sQuery(id+"F0.wireOp",EDGE,"E2"),sQuery(id+"F0.wireOp",EDGE,"E3"),sQuery(id+"F0.wireOp",EDGE,"E4.trimOffspring"),sQuery(id+"F0.wireOp",EDGE,"E5"),sQuery(id+"F0.wireOp",EDGE,"E6"),sQuery(id+"F0.wireOp",EDGE,"E8.MirrorCS"),sQuery(id+"F0.wireOp",EDGE,"E16.MirrorCS"),sQuery(id+"F0.wireOp",EDGE,"E17.MirrorCS"),sQuery(id+"F0.wireOp",EDGE,"E18.MirrorCS"),sQuery(id+"F0.wireOp",EDGE,"E19.MirrorCS"),sQuery(id+"F0.wireOp",EDGE,"E21.MirrorCS"),sQuery(id+"F0.wireOp",EDGE,"E25.MirrorCS"),sQuery(id+"F0.wireOp",EDGE,"E27.MirrorCS"),sQuery(id+"F0.wireOp",EDGE,"E28.MirrorCS"),sQuery(id+"F0.wireOp",EDGE,"E30.MirrorCS")])],"isStart":false}),makeQuery(id+"F2.opExtrude","SWEPT_FACE",FACE,{"disambiguationData":[OSD([sQuery(id+"F0.wireOp",EDGE,"E15.trimOffspring")])]})]});
            var Q102;
            Q102=makeQuery(id+"F2.boolean.opBoolean","INTERSECT",EDGE,{"derivedFrom":[makeQuery(id+"F1.opExtrude","CAP_FACE",FACE,{"disambiguationData":[OSD([sQuery(id+"F0.wireOp",EDGE,"E1.0"),sQuery(id+"F0.wireOp",EDGE,"E1.1"),sQuery(id+"F0.wireOp",EDGE,"E1.2"),sQuery(id+"F0.wireOp",EDGE,"E2"),sQuery(id+"F0.wireOp",EDGE,"E3"),sQuery(id+"F0.wireOp",EDGE,"E4.trimOffspring"),sQuery(id+"F0.wireOp",EDGE,"E5"),sQuery(id+"F0.wireOp",EDGE,"E6"),sQuery(id+"F0.wireOp",EDGE,"E8.MirrorCS"),sQuery(id+"F0.wireOp",EDGE,"E16.MirrorCS"),sQuery(id+"F0.wireOp",EDGE,"E17.MirrorCS"),sQuery(id+"F0.wireOp",EDGE,"E18.MirrorCS"),sQuery(id+"F0.wireOp",EDGE,"E19.MirrorCS"),sQuery(id+"F0.wireOp",EDGE,"E21.MirrorCS"),sQuery(id+"F0.wireOp",EDGE,"E25.MirrorCS"),sQuery(id+"F0.wireOp",EDGE,"E27.MirrorCS"),sQuery(id+"F0.wireOp",EDGE,"E28.MirrorCS"),sQuery(id+"F0.wireOp",EDGE,"E30.MirrorCS")])],"isStart":false}),makeQuery(id+"F2.opExtrude","SWEPT_FACE",FACE,{"disambiguationData":[OSD([sQuery(id+"F0.wireOp",EDGE,"E11")])]})]});
            var Q103;
            Q103=makeQuery(id+"F2.opExtrude","SWEPT_EDGE",EDGE,{"disambiguationData":[OSD([sQuery(id+"F0.wireOp",EDGE,"E22.MirrorCS"),sQuery(id+"F0.wireOp",EDGE,"E27.MirrorCS")])]});
            var Q104;
            Q104=makeQuery(id+"F2.boolean.opBoolean","INTERSECT",EDGE,{"derivedFrom":[makeQuery(id+"F1.opExtrude","CAP_FACE",FACE,{"disambiguationData":[OSD([sQuery(id+"F0.wireOp",EDGE,"E1.0"),sQuery(id+"F0.wireOp",EDGE,"E1.1"),sQuery(id+"F0.wireOp",EDGE,"E1.2"),sQuery(id+"F0.wireOp",EDGE,"E2"),sQuery(id+"F0.wireOp",EDGE,"E3"),sQuery(id+"F0.wireOp",EDGE,"E4.trimOffspring"),sQuery(id+"F0.wireOp",EDGE,"E5"),sQuery(id+"F0.wireOp",EDGE,"E6"),sQuery(id+"F0.wireOp",EDGE,"E8.MirrorCS"),sQuery(id+"F0.wireOp",EDGE,"E16.MirrorCS"),sQuery(id+"F0.wireOp",EDGE,"E17.MirrorCS"),sQuery(id+"F0.wireOp",EDGE,"E18.MirrorCS"),sQuery(id+"F0.wireOp",EDGE,"E19.MirrorCS"),sQuery(id+"F0.wireOp",EDGE,"E21.MirrorCS"),sQuery(id+"F0.wireOp",EDGE,"E25.MirrorCS"),sQuery(id+"F0.wireOp",EDGE,"E27.MirrorCS"),sQuery(id+"F0.wireOp",EDGE,"E28.MirrorCS"),sQuery(id+"F0.wireOp",EDGE,"E30.MirrorCS")])],"isStart":false}),makeQuery(id+"F2.opExtrude","SWEPT_FACE",FACE,{"disambiguationData":[OSD([sQuery(id+"F0.wireOp",EDGE,"E22.MirrorCS")])]})]});
            var Q105;
            Q105=makeQuery(id+"F4.boolean.opBoolean","INTERSECT",EDGE,{"derivedFrom":[makeQuery(id+"F1.opExtrude","CAP_FACE",FACE,{"disambiguationData":[OSD([sQuery(id+"F0.wireOp",EDGE,"E1.0"),sQuery(id+"F0.wireOp",EDGE,"E1.1"),sQuery(id+"F0.wireOp",EDGE,"E1.2"),sQuery(id+"F0.wireOp",EDGE,"E2"),sQuery(id+"F0.wireOp",EDGE,"E3"),sQuery(id+"F0.wireOp",EDGE,"E4.trimOffspring"),sQuery(id+"F0.wireOp",EDGE,"E5"),sQuery(id+"F0.wireOp",EDGE,"E6"),sQuery(id+"F0.wireOp",EDGE,"E8.MirrorCS"),sQuery(id+"F0.wireOp",EDGE,"E16.MirrorCS"),sQuery(id+"F0.wireOp",EDGE,"E17.MirrorCS"),sQuery(id+"F0.wireOp",EDGE,"E18.MirrorCS"),sQuery(id+"F0.wireOp",EDGE,"E19.MirrorCS"),sQuery(id+"F0.wireOp",EDGE,"E21.MirrorCS"),sQuery(id+"F0.wireOp",EDGE,"E25.MirrorCS"),sQuery(id+"F0.wireOp",EDGE,"E27.MirrorCS"),sQuery(id+"F0.wireOp",EDGE,"E28.MirrorCS"),sQuery(id+"F0.wireOp",EDGE,"E30.MirrorCS")])],"isStart":true}),makeQuery(id+"F4.opExtrude","SWEPT_FACE",FACE,{"disambiguationData":[OSD([sQuery(id+"F3.wireOp",EDGE,"E32.left")])]})]});
            var Q106;
            Q106=makeQuery(id+"F1.opExtrude","CAP_EDGE",EDGE,{"disambiguationData":[OSD([sQuery(id+"F0.wireOp",EDGE,"E5")])],"isStart":true});
            var Q107;
            Q107=makeQuery(id+"F1.opExtrude","CAP_EDGE",EDGE,{"disambiguationData":[OSD([sQuery(id+"F0.wireOp",EDGE,"E16.MirrorCS")])],"isStart":true});
            fillet(context, id + "F5", {"entities" : qUnion([Q0, Q1, Q2, Q3, Q4, Q5, Q6, Q7, Q8, Q9, Q10, Q11, Q12, Q13, Q14, Q15, Q16, Q17, Q18, Q19, Q20, Q21, Q22, Q23, Q24, Q25, Q26, Q27, Q28, Q29, Q30, Q31, Q32, Q33, Q34, Q35, Q36, Q37, Q38, Q39, Q40, Q41, Q42, Q43, Q44, Q45, Q46, Q47, Q48, Q49, Q50, Q51, Q52, Q53, Q54, Q55, Q56, Q57, Q58, Q59, Q60, Q61, Q62, Q63, Q64, Q65, Q66, Q67, Q68, Q69, Q70, Q71, Q72, Q73, Q74, Q75, Q76, Q77, Q78, Q79, Q80, Q81, Q82, Q83, Q84, Q85, Q86, Q87, Q88, Q89, Q90, Q91, Q92, Q93, Q94, Q95, Q96, Q97, Q98, Q99, Q100, Q101, Q102, Q103, Q104, Q105, Q106, Q107]), "radius" : 1 * mm, "tangentPropagation" : true, "allowEdgeOverflow" : false});
        }
    });
